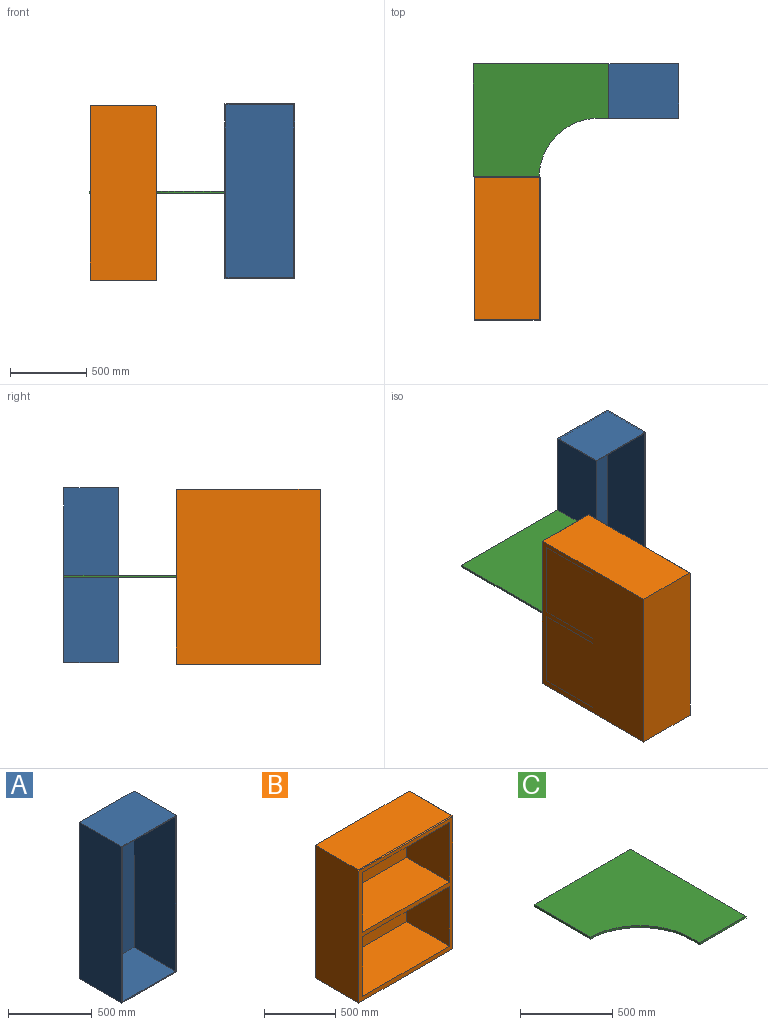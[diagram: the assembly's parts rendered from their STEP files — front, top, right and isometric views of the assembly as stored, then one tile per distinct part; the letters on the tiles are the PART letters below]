
ASSEMBLY  parts=3 mates=2
PART A: 11 faces, bbox 457.2x355.6x1143 mm
  f0: plane 1143x457.2mm, normal (0,-1,0), area 20161.3mm2, adj f1,f3,f4,f5,f6,f7,f8,f9
  f1: plane 1143x355.6mm, normal (1,0,0), area 406450.8mm2, adj f0,f2,f4,f5
  f2: plane 1143x457.2mm, normal (0,1,0), area 522579.6mm2, adj f1,f3,f4,f5
  f3: plane 1143x355.6mm, normal (-1,0,0), area 406450.8mm2, adj f0,f2,f4,f5
  f4: plane 457.2x355.6mm, normal (0,0,1), area 162580.3mm2, adj f0,f1,f2,f3
  f5: plane 457.2x355.6mm, normal (0,0,-1), area 162580.3mm2, adj f0,f1,f2,f3
  f6: plane 1130.3x349.25mm, normal (1,0,0), area 394757.3mm2, adj f0,f7,f9,f10
  f7: plane 444.5x349.25mm, normal (0,0,1), area 155241.6mm2, adj f0,f6,f8,f10
  f8: plane 1130.3x349.25mm, normal (-1,0,0), area 394757.3mm2, adj f0,f7,f9,f10
  f9: plane 444.5x349.25mm, normal (0,0,-1), area 155241.6mm2, adj f0,f6,f8,f10
  f10: plane 1130.3x444.5mm, normal (0,-1,0), area 502418.3mm2, adj f6,f7,f8,f9
PART B: 19 faces, bbox 939.8x431.8x1143 mm
  f0: plane 1136.65x933.45mm, normal (0,-1,0), area 172620.6mm2, adj f3,f5,f6,f7,f8,f9,f11,f12
  f1: plane 1136.65x425.45mm, normal (1,0,0), area 483587.7mm2, adj f2,f5,f17,f18
  f2: plane 1143x939.8mm, normal (0,1,0), area 1074171.2mm2, adj f1,f3,f4,f5,f18
  f3: plane 1143x431.8mm, normal (-1,0,0), area 493527.2mm2, adj f0,f2,f4,f5,f16
  f4: plane 933.45x425.45mm, normal (0,0,1), area 397136.3mm2, adj f2,f3,f16,f18
  f5: plane 939.8x431.8mm, normal (0,0,-1), area 405785.5mm2, adj f0,f1,f2,f3,f17
  f6: plane 863.6x425.45mm, normal (0,0,-1), area 367418.6mm2, adj f0,f7,f9,f10
  f7: plane 514.35x425.45mm, normal (1,0,0), area 218830.2mm2, adj f0,f6,f8,f10
  f8: plane 863.6x425.45mm, normal (0,0,1), area 367418.6mm2, adj f0,f7,f9,f10
  f9: plane 514.35x425.45mm, normal (-1,0,0), area 218830.2mm2, adj f0,f6,f8,f10
  f10: plane 863.6x514.35mm, normal (0,-1,0), area 444192.7mm2, adj f6,f7,f8,f9
  f11: plane 514.35x425.45mm, normal (1,0,0), area 218830.2mm2, adj f0,f12,f14,f15
  f12: plane 863.6x425.45mm, normal (0,0,1), area 367418.6mm2, adj f0,f11,f13,f15
  f13: plane 514.35x425.45mm, normal (-1,0,0), area 218830.2mm2, adj f0,f12,f14,f15
  f14: plane 863.6x425.45mm, normal (0,0,-1), area 367418.6mm2, adj f0,f11,f13,f15
  f15: plane 863.6x514.35mm, normal (0,-1,0), area 444192.7mm2, adj f11,f12,f13,f14
  f16: plane 936.63x6.35mm, normal (0,-0.71,0.71), area 8396.9mm2, adj f0,f3,f4,f17,f18
  f17: plane 1139.83x6.35mm, normal (0.71,-0.71,0), area 10221.7mm2, adj f0,f1,f5,f16,f18
  f18: plane 428.63x6.35mm, normal (0.71,0,0.71), area 3834.9mm2, adj f1,f2,f4,f16,f17
PART C: 8 faces, bbox 736.6x889x12.7 mm
  f0: plane 431.8x12.7mm, normal (-1,0,0), area 5483.9mm2, adj f1,f5,f6,f7
  f1: cylinder r=389.41mm len=381mm, axis (0,0,-1), area 7557mm2, adj f0,f2,f6,f7
  f2: plane 76.2x12.7mm, normal (-1,0,0), area 967.7mm2, adj f1,f3,f6,f7
  f3: plane 355.6x12.7mm, normal (0,-1,0), area 4516.1mm2, adj f2,f4,f6,f7
  f4: plane 889x12.7mm, normal (1,0,0), area 11290.3mm2, adj f3,f5,f6,f7
  f5: plane 736.6x12.7mm, normal (0,1,0), area 9354.8mm2, adj f0,f4,f6,f7
  f6: plane 889x736.6mm, normal (0,0,1), area 513118.6mm2, adj f0,f1,f2,f3,f4,f5
  f7: plane 889x736.6mm, normal (0,0,-1), area 513118.6mm2, adj f0,f1,f2,f3,f4,f5
PLACE A t=(150.57,-1131.19,184.26)mm
PLACE B rot(axis=(0,0,1),90deg) t=(-744.78,-2159.89,174.73)mm
PLACE C rot(axis=(0,0,1),90deg) t=(-751.13,-1791.59,743.06)mm
MATE fastened C.f3 <-> A.f3  axis (1,0,0) through (-78.03,-953.39,755.76)mm
MATE fastened B.f1 <-> C.f0  axis (0,1,0) through (-535.23,-1689.99,743.06)mm
